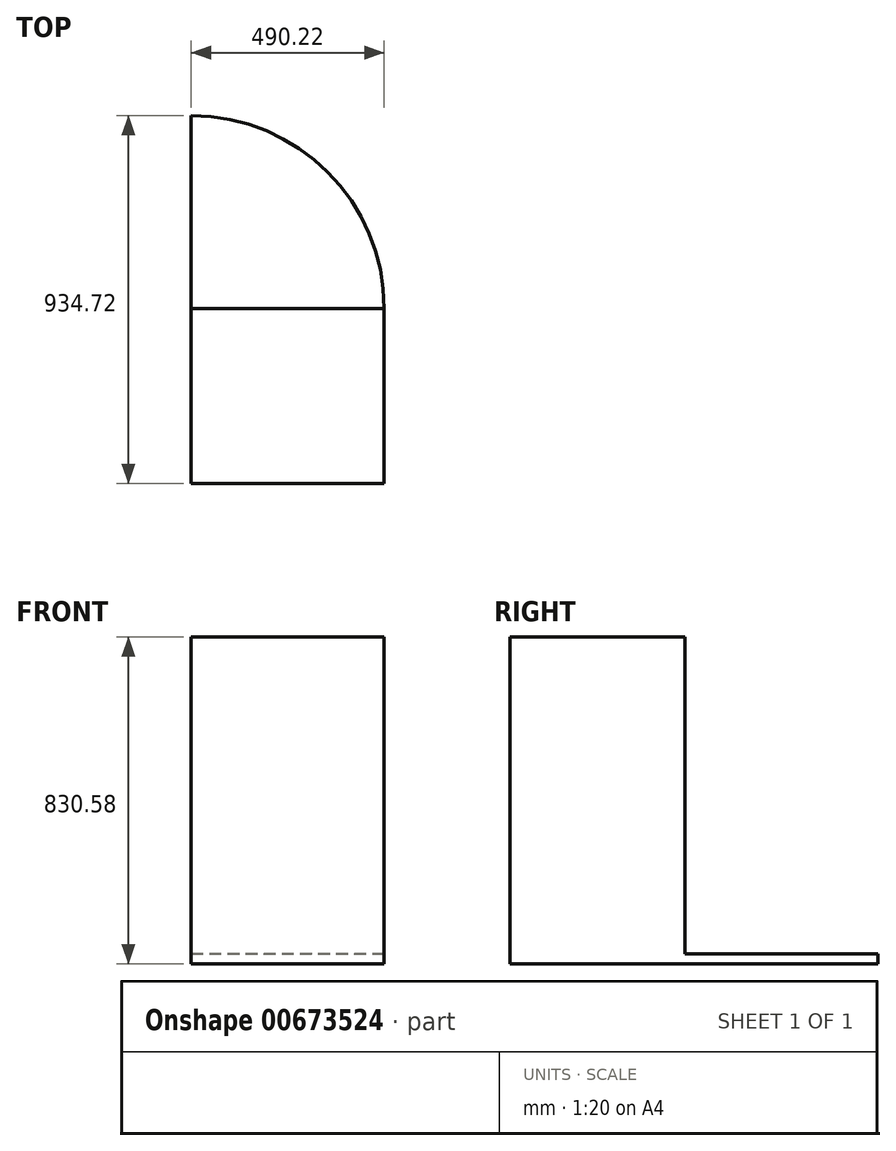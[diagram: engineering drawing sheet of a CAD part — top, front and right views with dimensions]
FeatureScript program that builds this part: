
annotation { "Feature Type Name" : "Feature", "Feature Type Description" : "" }
export const myFeature = defineFeature(function(context is Context, id is Id, definition is map)
    precondition{}
    {
        {
            var Q0;
            Q0=qCreatedBy(makeId("Top.planeOp"),FACE);
            var sketch = newSketch(context, id + "F0", { "sketchPlane" : qUnion([Q0])});
            skLineSegment(sketch, "E0.bottom", {"start": v(245.11, 222.25) * mm, "end": v(-245.1, 222.25) * mm});
            skLineSegment(sketch, "E0.top", {"start": v(245.11, -222.25) * mm, "end": v(-245.11, -222.25) * mm});
            skLineSegment(sketch, "E0.left", {"start": v(245.11, 222.25) * mm, "end": v(245.11, -222.25) * mm});
            skLineSegment(sketch, "E0.right", {"start": v(-245.1, 222.25) * mm, "end": v(-245.11, -222.25) * mm});
            skPoint(sketch, "E0.middle", {"position": v(0, 0) * mm});
            skSolve(sketch);
        }
        {
            var Q0;
            Q0=makeQuery(id+"F0.imprint","IMPRINT",FACE,{"disambiguationData":[TD([[makeQuery(id+"F0.imprint","IMPRINT",EDGE,{"derivedFrom":sQuery(id+"F0.wireOp",EDGE,"E0.bottom")}),1.0]])]});
            extrude(context, id + "F1", {"entities" : qUnion([Q0]), "flatOperationType" : FlatOperationType.REMOVE, "depth" : 830.58 * mm, "offsetDistance" : 25.4 * mm, "domain" : OperationDomain.MODEL});
        }
        {
            var Q0;
            Q0=makeQuery(id+"F1.opExtrude","CAP_FACE",FACE,{"disambiguationData":[OSD([sQuery(id+"F0.wireOp",EDGE,"E0.bottom"),sQuery(id+"F0.wireOp",EDGE,"E0.top"),sQuery(id+"F0.wireOp",EDGE,"E0.left"),sQuery(id+"F0.wireOp",EDGE,"E0.right")])],"isStart":true});
            var sketch = newSketch(context, id + "F2", { "sketchPlane" : qUnion([Q0])});
            skArc(sketch, "E1", {"start": v(-245.1, -712.47) * mm, "mid": v(101.53, -568.89) * mm, "end": v(245.11, -222.25) * mm});
            skLineSegment(sketch, "E2", {"start": v(-245.1, -712.47) * mm, "end": v(-245.1, -222.25) * mm});
            skLineSegment(sketch, "E3", {"start": v(-245.1, -222.25) * mm, "end": v(245.11, -222.25) * mm});
            skSolve(sketch);
        }
        {
            var Q0;
            Q0=makeQuery(id+"F2.imprint","IMPRINT",FACE,{"disambiguationData":[TD([[makeQuery(id+"F2.imprint","IMPRINT",EDGE,{"derivedFrom":sQuery(id+"F2.wireOp",EDGE,"E1")}),1.0]])]});
            extrude(context, id + "F3", {"entities" : qUnion([Q0]), "operationType" : NewBodyOperationType.ADD, "oppositeDirection" : true, "depth" : 25.4 * mm, "offsetDistance" : 25.4 * mm});
        }
    });
